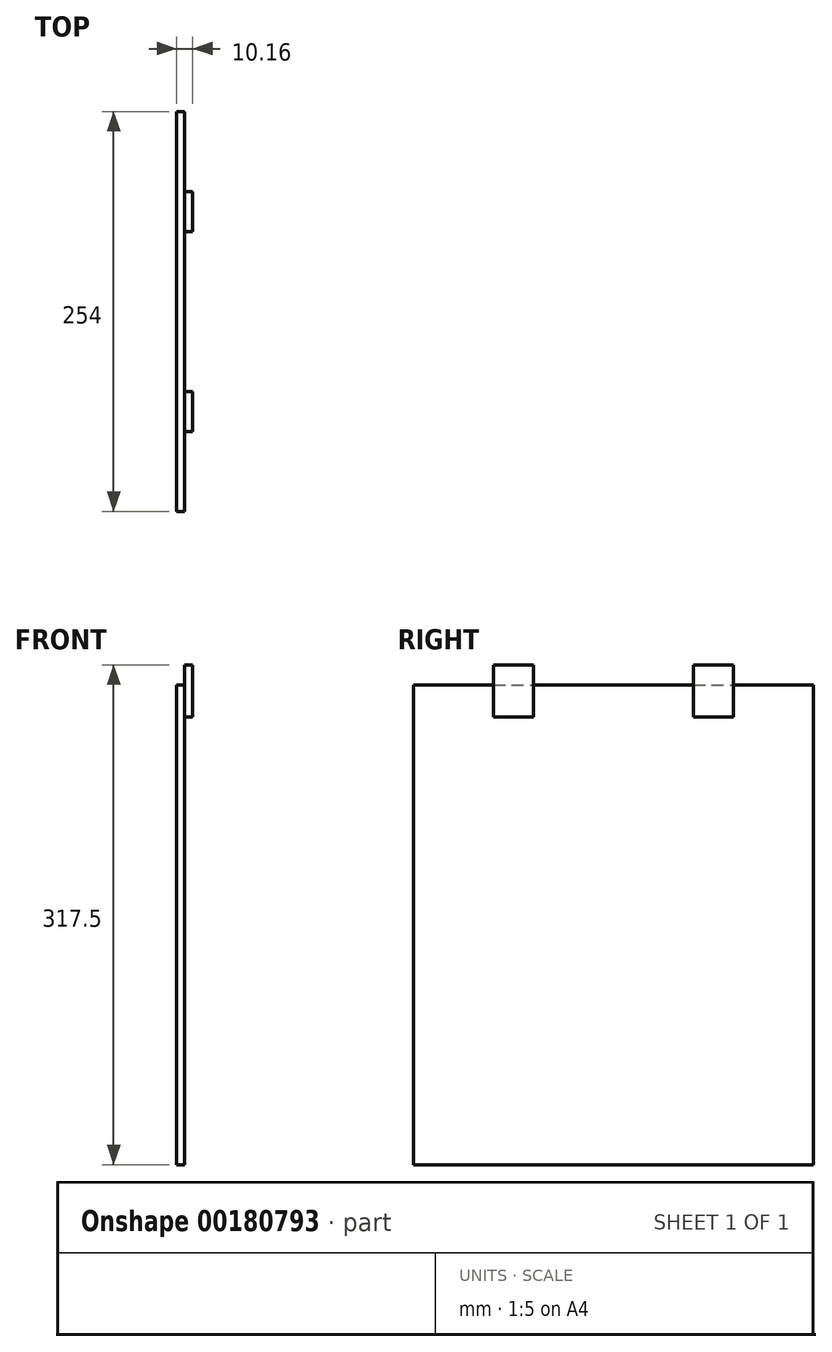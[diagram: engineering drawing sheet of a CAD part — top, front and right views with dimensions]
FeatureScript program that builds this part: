
annotation { "Feature Type Name" : "Feature", "Feature Type Description" : "" }
export const myFeature = defineFeature(function(context is Context, id is Id, definition is map)
    precondition{}
    {
        {
            var Q0;
            Q0=qCreatedBy(makeId("Front.planeOp"),FACE);
            var sketch = newSketch(context, id + "F0", { "sketchPlane" : qUnion([Q0])});
            skLineSegment(sketch, "E0", {"start": v(0, 166.4) * mm, "end": v(0, -138.4) * mm});
            skLineSegment(sketch, "E1", {"start": v(0, -138.4) * mm, "end": v(-5.08, -138.4) * mm});
            skLineSegment(sketch, "E2", {"start": v(-5.08, -138.4) * mm, "end": v(-5.08, 166.4) * mm});
            skLineSegment(sketch, "E3", {"start": v(-5.08, 166.4) * mm, "end": v(0, 166.4) * mm});
            skSolve(sketch);
        }
        {
            var Q0;
            Q0=makeQuery(id+"F0.imprint","IMPRINT",FACE,{"disambiguationData":[TD([[makeQuery(id+"F0.imprint","IMPRINT",EDGE,{"derivedFrom":sQuery(id+"F0.wireOp",EDGE,"E0")}),-1.0]])]});
            extrude(context, id + "F1", {"entities" : qUnion([Q0]), "depth" : 50.8 * mm});
        }
        {
            var Q0;
            Q0=makeQuery(id+"F1.opExtrude","CAP_FACE",FACE,{"disambiguationData":[OSD([sQuery(id+"F0.wireOp",EDGE,"E0"),sQuery(id+"F0.wireOp",EDGE,"E1"),sQuery(id+"F0.wireOp",EDGE,"E2"),sQuery(id+"F0.wireOp",EDGE,"E3")])],"isStart":false});
            var sketch = newSketch(context, id + "F2", { "sketchPlane" : qUnion([Q0])});
            skLineSegment(sketch, "E4", {"start": v(0, 166.4) * mm, "end": v(0, 179.1) * mm});
            skLineSegment(sketch, "E5", {"start": v(0, 179.1) * mm, "end": v(5.08, 179.1) * mm});
            skLineSegment(sketch, "E6", {"start": v(5.08, 179.1) * mm, "end": v(5.08, 146.07) * mm});
            skLineSegment(sketch, "E7", {"start": v(5.08, 146.07) * mm, "end": v(0, 146.07) * mm});
            skSolve(sketch);
        }
        {
            var Q0;
            {var subQ1=sQuery(id+"F2.wireOp",EDGE,"E4");Q0=makeQuery(id+"F2.imprint","IMPRINT",FACE,{"disambiguationData":[TD([[makeQuery(id+"F2.imprint","IMPRINT",EDGE,{"derivedFrom":subQ1}),-1.0]])]});}
            var Q1;
            {var subQ0=makeQuery(id+"F1.opExtrude","CAP_EDGE",EDGE,{"disambiguationData":[OSD([sQuery(id+"F0.wireOp",EDGE,"E1")])],"isStart":false});Q1=makeQuery(id+"F2.imprint","IMPRINT",FACE,{"disambiguationData":[TD([[makeQuery(id+"F2.imprint","IMPRINT",EDGE,{"derivedFrom":subQ0}),-1.0]])]});}
            extrude(context, id + "F3", {"entities" : qUnion([Q0, Q1]), "operationType" : NewBodyOperationType.ADD, "depth" : 25.4 * mm});
        }
        {
            var Q0;
            Q0=makeQuery(id+"F3.opExtrude","CAP_FACE",FACE,{"disambiguationData":[OSD([sQuery(id+"F0.wireOp",EDGE,"E0"),sQuery(id+"F0.wireOp",EDGE,"E1"),sQuery(id+"F0.wireOp",EDGE,"E2"),sQuery(id+"F0.wireOp",EDGE,"E3"),sQuery(id+"F2.wireOp",EDGE,"E4"),sQuery(id+"F2.wireOp",EDGE,"E5"),sQuery(id+"F2.wireOp",EDGE,"E6"),sQuery(id+"F2.wireOp",EDGE,"E7")])],"isStart":false});
            var sketch = newSketch(context, id + "F4", { "sketchPlane" : qUnion([Q0])});
            skLineSegment(sketch, "E8", {"start": v(-5.08, 166.4) * mm, "end": v(0, 166.4) * mm});
            skLineSegment(sketch, "E9", {"start": v(0, 166.4) * mm, "end": v(0, -138.4) * mm});
            skLineSegment(sketch, "E10", {"start": v(0, -138.4) * mm, "end": v(-5.08, -138.4) * mm});
            skLineSegment(sketch, "E11", {"start": v(-5.08, -138.4) * mm, "end": v(-5.08, 166.4) * mm});
            skSolve(sketch);
        }
        {
            var Q0;
            {var subQ2=sQuery(id+"F4.wireOp",EDGE,"E8");Q0=makeQuery(id+"F4.imprint","IMPRINT",FACE,{"disambiguationData":[TD([[makeQuery(id+"F4.imprint","IMPRINT",EDGE,{"derivedFrom":subQ2}),-1.0]])]});}
            extrude(context, id + "F5", {"entities" : qUnion([Q0]), "operationType" : NewBodyOperationType.ADD, "depth" : 101.6 * mm});
        }
        {
            var Q0;
            Q0=makeQuery(id+"F5.opExtrude","CAP_FACE",FACE,{"disambiguationData":[OSD([sQuery(id+"F4.wireOp",EDGE,"E8"),sQuery(id+"F4.wireOp",EDGE,"E9"),sQuery(id+"F4.wireOp",EDGE,"E10"),sQuery(id+"F4.wireOp",EDGE,"E11")])],"isStart":false});
            var sketch = newSketch(context, id + "F6", { "sketchPlane" : qUnion([Q0])});
            skLineSegment(sketch, "E12", {"start": v(0, 166.4) * mm, "end": v(0, 179.1) * mm});
            skLineSegment(sketch, "E13", {"start": v(0, 179.1) * mm, "end": v(5.08, 179.1) * mm});
            skLineSegment(sketch, "E14", {"start": v(5.08, 179.1) * mm, "end": v(5.08, 146.07) * mm});
            skLineSegment(sketch, "E15", {"start": v(5.08, 146.07) * mm, "end": v(0, 146.07) * mm});
            skSolve(sketch);
        }
        {
            var Q0;
            {var subQ1=sQuery(id+"F6.wireOp",EDGE,"E12");Q0=makeQuery(id+"F6.imprint","IMPRINT",FACE,{"disambiguationData":[TD([[makeQuery(id+"F6.imprint","IMPRINT",EDGE,{"derivedFrom":subQ1}),-1.0]])]});}
            var Q1;
            {var subQ3=makeQuery(id+"F5.opExtrude","CAP_EDGE",EDGE,{"disambiguationData":[OSD([sQuery(id+"F4.wireOp",EDGE,"E8")])],"isStart":false});Q1=makeQuery(id+"F6.imprint","IMPRINT",FACE,{"disambiguationData":[TD([[makeQuery(id+"F6.imprint","IMPRINT",EDGE,{"derivedFrom":subQ3}),-1.0]])]});}
            extrude(context, id + "F7", {"entities" : qUnion([Q0, Q1]), "operationType" : NewBodyOperationType.ADD, "depth" : 25.4 * mm});
        }
        {
            var Q0;
            Q0=makeQuery(id+"F7.opExtrude","CAP_FACE",FACE,{"disambiguationData":[OSD([sQuery(id+"F4.wireOp",EDGE,"E8"),sQuery(id+"F4.wireOp",EDGE,"E9"),sQuery(id+"F4.wireOp",EDGE,"E10"),sQuery(id+"F4.wireOp",EDGE,"E11"),sQuery(id+"F6.wireOp",EDGE,"E12"),sQuery(id+"F6.wireOp",EDGE,"E13"),sQuery(id+"F6.wireOp",EDGE,"E14"),sQuery(id+"F6.wireOp",EDGE,"E15")])],"isStart":false});
            var sketch = newSketch(context, id + "F8", { "sketchPlane" : qUnion([Q0])});
            skLineSegment(sketch, "E16", {"start": v(-5.08, 166.4) * mm, "end": v(0, 166.4) * mm});
            skLineSegment(sketch, "E17", {"start": v(0, 166.4) * mm, "end": v(0, -138.4) * mm});
            skLineSegment(sketch, "E18", {"start": v(0, -138.4) * mm, "end": v(-5.08, -138.4) * mm});
            skLineSegment(sketch, "E19", {"start": v(-5.08, -138.4) * mm, "end": v(-5.08, 166.4) * mm});
            skSolve(sketch);
        }
        {
            var Q0;
            {var subQ3=sQuery(id+"F8.wireOp",EDGE,"E16");Q0=makeQuery(id+"F8.imprint","IMPRINT",FACE,{"disambiguationData":[TD([[makeQuery(id+"F8.imprint","IMPRINT",EDGE,{"derivedFrom":subQ3}),-1.0]])]});}
            extrude(context, id + "F9", {"entities" : qUnion([Q0]), "operationType" : NewBodyOperationType.ADD, "depth" : 50.8 * mm});
        }
    });
